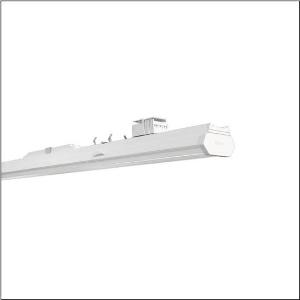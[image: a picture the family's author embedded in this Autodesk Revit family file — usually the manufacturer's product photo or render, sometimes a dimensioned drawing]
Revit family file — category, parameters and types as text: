
# Revit family: licross_21_protected_mo_52tp11dn48xg
name_source: partatom
category: Lighting Fixtures
units: mm (PartAtom-declared; Revit-internal decimal feet)

## family parameters
Cut with Voids When Loaded = No
Host = Face
Light Source = No
Part Type = Normal
Room Calculation Point = No
Round Connector Dimension = Use Diameter
Shared = No

## types (1)
- --- (1 x LED, 8000 lm, 45.5 W, 4000K)
    Apparent Load = 46 VA
    CIE Flux Codes = 83 94 98 100 100
    Color Rendering = 80
    Color Temperature = 4000K
    Default Elevation = 1800 mm
    Description = Licross 21 Protected MO, luminaire insert, of sheet steel, galvanised, coil coated, white, length: 1.500mm, width: 90mm, height: 103mm, LED rated luminous flux: 8.000lm, light colour: 840, SDCM (Standard Deviation of Colour Matching)MacAdam ≤ 3 SDCM (initial), control gear: DALI 2, with plug, 5-pole, with phase selection, mains connection: 220..240V, AC, 50/60Hz, rated input power: 46W, internal wiring halogen-free, primary light control with lens, of plastic, primary optical cover: cover, of PMMA, light emission: direct distribution, primary light characteristic: symmetric, protection rating (complete): IP64, insulation class (complete): insulation class I (protective earthing), certification: CE, ENEC, VDE, UKCA, protection symbol: D if used in an environment with conductive dust loads with corresponding accessories, impact resistance: IK06, permissible ambient temperature for indoor applications: -25..+45°C, corresponds to IFS (International Featured Standards) requirements for safety and quality in the food industry, reducing of maximum allowable ambient temperature of 5°C with ceiling mounting, LABS conformity tested according to VDMA 24364:2018-05, The light source and the operating device comply with the requirements of the Ecodesign Regulation (EU) 2019/2020 and are replaceable in accordance with this regulation, packaging unit: 1 piece
    Height = 92 mm
    Lamp = 1 x LED
    Lamp Light Flux = 8000 lm
    Lamp Power = 45.5 W
    Lamp count = 1
    Length = 1500 mm
    Luminous efficacy = 176 lm/W
    Manufacturer = Siteco
    ModVariant = No
    Model = 52TP11DN48XG
    Mounting Place = Ceiling
    Mounting Type = Pendant
    Number of Poles = 1
    OnlyDefault = Yes
    Power Factor = 1
    Product Name = Licross 21 Protected MO
    Product group = luminaire insert | ceiling pendant
    ProductGroupID = 901
    Protection Class = Protection class I
    Protection Degree = IP 64
    RLX_Detail_Level = 1
    RLX_Emergency_Light_Flux = 0 lm
    RLX_Emergency_Type = 0
    RLX_Emergency_Type_DB = No
    RlxData = <blob elided: 24369 chars, md5=0d7182fc>
    Socket = socket
    Standby Power = 0 W
    System Light Flux = 8000 lm
    System Power = 46 W
    Type Comments = factory setting: luminous flux: 100 % | dim-lin: 254 | 307 mA
    Type Image = l_1256148.jpg
    URL = http://relux.com
    VarID = @adj_129897
    Voltage = 0 V
    Weight = 0.00 kg
    Width = 88 mm

## geometry (parser evidence)
native form markers: Blend x4, Sweep x12
no freeform markers — native parametric forms only
